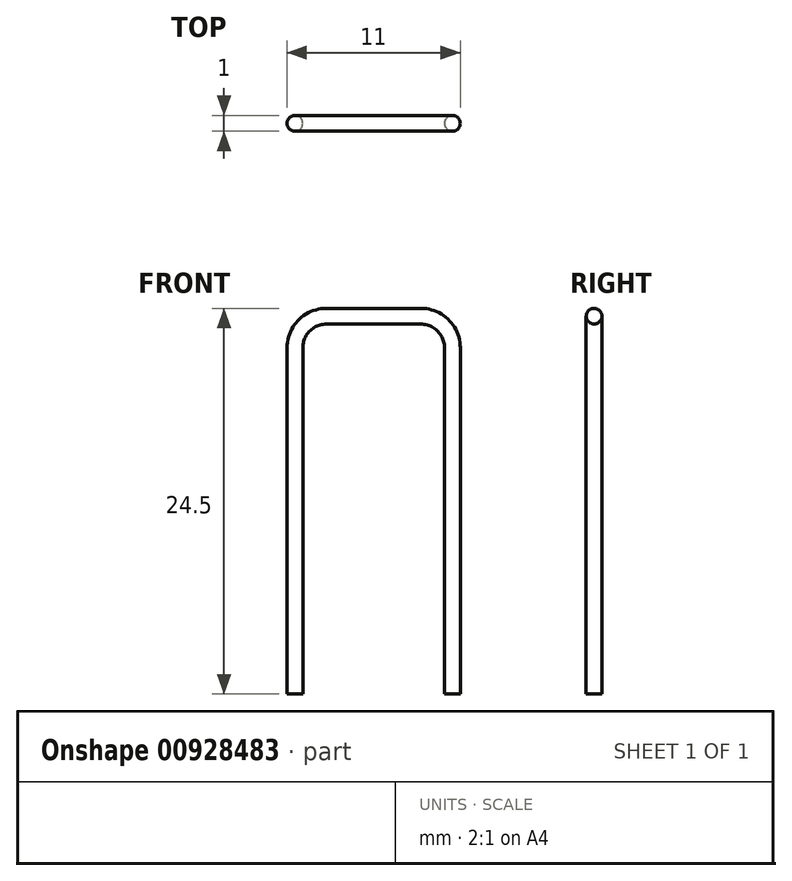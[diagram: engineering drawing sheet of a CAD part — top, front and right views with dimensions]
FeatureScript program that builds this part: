
annotation { "Feature Type Name" : "Feature", "Feature Type Description" : "" }
export const myFeature = defineFeature(function(context is Context, id is Id, definition is map)
    precondition{}
    {
        {
            var Q0;
            Q0=qCreatedBy(makeId("Front.planeOp"),FACE);
            var sketch = newSketch(context, id + "F0", { "sketchPlane" : qUnion([Q0])});
            skLineSegment(sketch, "E0.bottom", {"start": v(3, 24) * mm, "end": v(-3, 24) * mm});
            skPoint(sketch, "E0.middle", {"position": v(0, 0) * mm});
            skPoint(sketch, "E0.top.end.orphan", {"position": v(-5, -24) * mm});
            skPoint(sketch, "E0.top.start.orphan", {"position": v(5, -24) * mm});
            skLineSegment(sketch, "E1", {"start": v(-5, 22) * mm, "end": v(-5, 0) * mm});
            skLineSegment(sketch, "E2", {"start": v(5, 22) * mm, "end": v(5, 0) * mm});
            skPoint(sketch, "E3.visualSharp", {"position": v(5, 24) * mm});
            skArc(sketch, "E3.filletArc", {"start": v(5, 22) * mm, "mid": v(4.41, 23.41) * mm, "end": v(3, 24) * mm});
            skPoint(sketch, "E4.visualSharp", {"position": v(-5, 24) * mm});
            skArc(sketch, "E4.filletArc", {"start": v(-3, 24) * mm, "mid": v(-4.41, 23.41) * mm, "end": v(-5, 22) * mm});
            skSolve(sketch);
        }
        {
            var Q0;
            Q0=qCreatedBy(makeId("Top.planeOp"),FACE);
            var sketch = newSketch(context, id + "F1", { "sketchPlane" : qUnion([Q0])});
            skCircle(sketch, "E5", {"center": v(5, 0) * mm, "radius": 0.5 * mm});
            skSolve(sketch);
        }
        {
            var Q0;
            Q0=makeQuery(id+"F1.imprint","IMPRINT",FACE,{"disambiguationData":[TD([[makeQuery(id+"F1.imprint","IMPRINT",EDGE,{"derivedFrom":sQuery(id+"F1.wireOp",EDGE,"E5")}),1.0]])]});
            var Q1;
            Q1=sQuery(id+"F0.wireOp",EDGE,"E2");
            var Q2;
            Q2=sQuery(id+"F0.wireOp",EDGE,"E3.filletArc");
            var Q3;
            Q3=sQuery(id+"F0.wireOp",EDGE,"E0.bottom");
            var Q4;
            Q4=sQuery(id+"F0.wireOp",EDGE,"E4.filletArc");
            var Q5;
            Q5=sQuery(id+"F0.wireOp",EDGE,"E1");
            sweep(context, id + "F2", {"profiles" : qUnion([Q0]), "path" : qUnion([Q1, Q2, Q3, Q4, Q5])});
        }
    });
